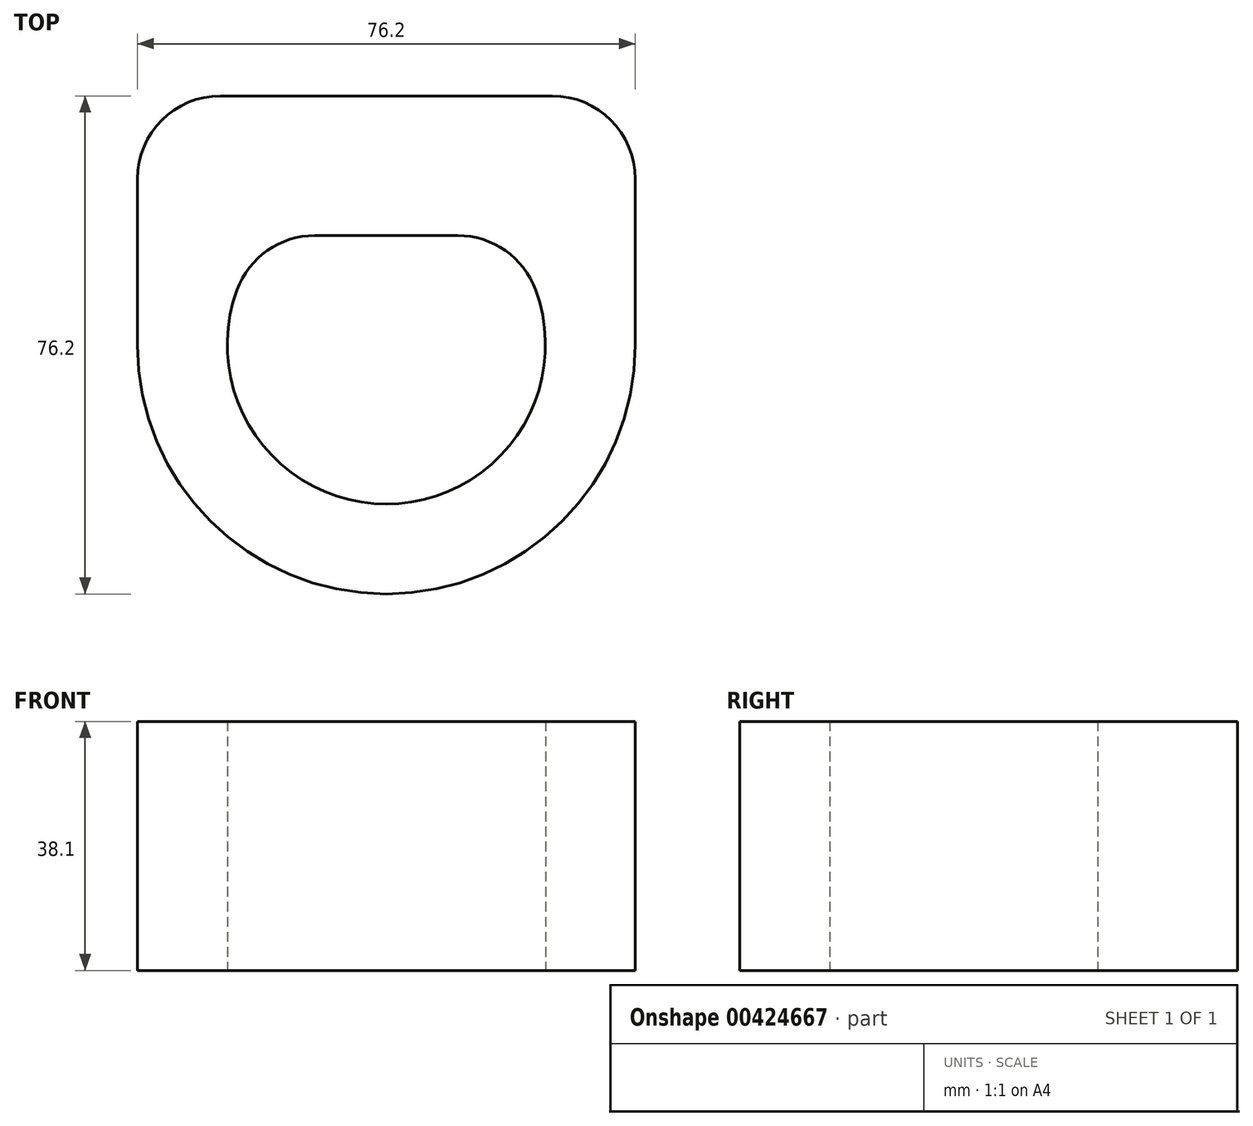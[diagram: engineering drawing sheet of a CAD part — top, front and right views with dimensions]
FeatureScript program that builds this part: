
annotation { "Feature Type Name" : "Feature", "Feature Type Description" : "" }
export const myFeature = defineFeature(function(context is Context, id is Id, definition is map)
    precondition{}
    {
        {
            var Q0;
            Q0=qCreatedBy(makeId("Top.planeOp"),FACE);
            var sketch = newSketch(context, id + "F0", { "sketchPlane" : qUnion([Q0])});
            skArc(sketch, "E0", {"start": v(-38.1, 0) * mm, "mid": v(0, -38.1) * mm, "end": v(38.1, 0) * mm});
            skPoint(sketch, "E1", {"position": v(0, 38.1) * mm});
            skLineSegment(sketch, "E2", {"start": v(0, 0) * mm, "end": v(38.1, 0) * mm, "construction": true});
            skLineSegment(sketch, "E3", {"start": v(0, 0) * mm, "end": v(-38.1, 0) * mm, "construction": true});
            skLineSegment(sketch, "E4", {"start": v(-38.1, 0) * mm, "end": v(-38.1, 25.4) * mm});
            skLineSegment(sketch, "E5", {"start": v(0, 38.1) * mm, "end": v(-25.4, 38.1) * mm});
            skLineSegment(sketch, "E6", {"start": v(38.1, 0) * mm, "end": v(38.1, 25.4) * mm});
            skLineSegment(sketch, "E7", {"start": v(0, 38.1) * mm, "end": v(25.4, 38.1) * mm});
            skPoint(sketch, "E8.visualSharp", {"position": v(-38.1, 38.1) * mm});
            skArc(sketch, "E8.filletArc", {"start": v(-25.4, 38.1) * mm, "mid": v(-34.38, 34.38) * mm, "end": v(-38.1, 25.4) * mm});
            skPoint(sketch, "E9.visualSharp", {"position": v(38.1, 38.1) * mm});
            skArc(sketch, "E9.filletArc", {"start": v(38.1, 25.4) * mm, "mid": v(34.38, 34.38) * mm, "end": v(25.4, 38.1) * mm});
            skArc(sketch, "E10", {"start": v(-22.85, 8.42) * mm, "mid": v(0, -24.35) * mm, "end": v(22.85, 8.42) * mm});
            skLineSegment(sketch, "E11", {"start": v(0, 0) * mm, "end": v(0, 16.73) * mm});
            skLineSegment(sketch, "E12", {"start": v(-10.93, 16.73) * mm, "end": v(10.93, 16.73) * mm});
            skPoint(sketch, "E13", {"position": v(0, 16.73) * mm});
            skPoint(sketch, "E14.orphan", {"position": v(0, 24.35) * mm});
            skPoint(sketch, "E15.visualSharp", {"position": v(-17.7, 16.73) * mm});
            skArc(sketch, "E15.filletArc", {"start": v(-10.93, 16.73) * mm, "mid": v(-18.2, 14.44) * mm, "end": v(-22.85, 8.42) * mm});
            skPoint(sketch, "E16.visualSharp", {"position": v(17.7, 16.73) * mm});
            skArc(sketch, "E16.filletArc", {"start": v(22.85, 8.42) * mm, "mid": v(18.2, 14.44) * mm, "end": v(10.93, 16.73) * mm});
            skSolve(sketch);
        }
        {
            var Q0;
            Q0=makeQuery(id+"F0.imprint","IMPRINT",FACE,{"disambiguationData":[TD([[makeQuery(id+"F0.imprint","IMPRINT",EDGE,{"derivedFrom":sQuery(id+"F0.wireOp",EDGE,"E0")}),1.0]])]});
            extrude(context, id + "F1", {"entities" : qUnion([Q0]), "depth" : 38.1 * mm});
        }
    });
